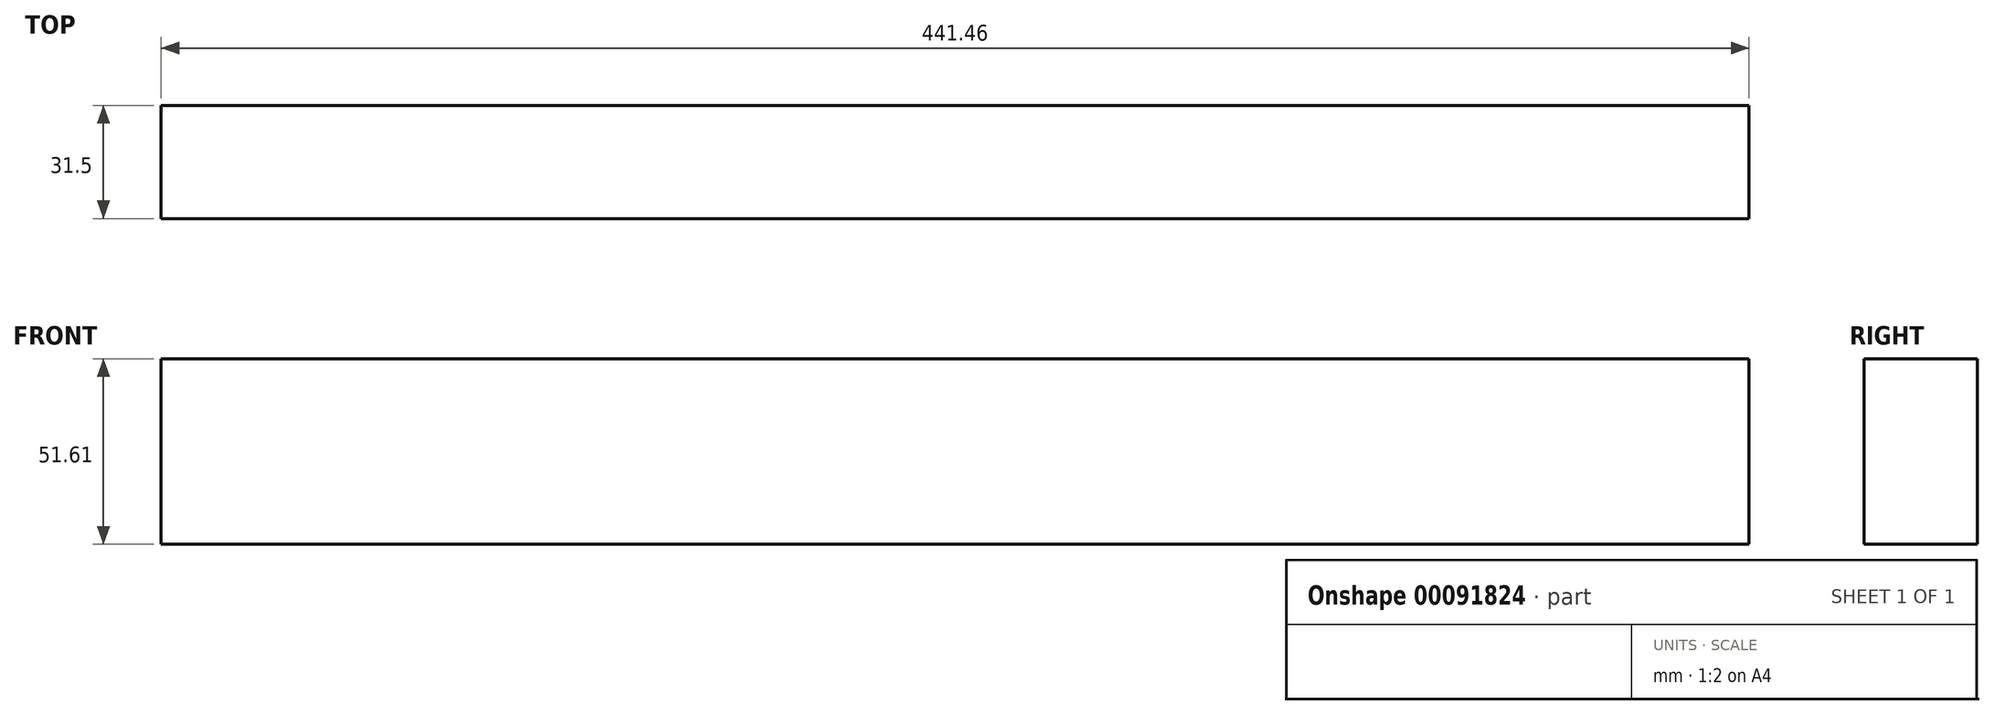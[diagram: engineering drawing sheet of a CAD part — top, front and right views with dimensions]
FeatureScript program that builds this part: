
annotation { "Feature Type Name" : "Feature", "Feature Type Description" : "" }
export const myFeature = defineFeature(function(context is Context, id is Id, definition is map)
    precondition{}
    {
        {
            var Q0;
            Q0=qCreatedBy(makeId("Top.planeOp"),FACE);
            var sketch = newSketch(context, id + "F0", { "sketchPlane" : qUnion([Q0])});
            skLineSegment(sketch, "E0.bottom", {"start": v(220.73, -15.75) * mm, "end": v(-220.73, -15.75) * mm});
            skLineSegment(sketch, "E0.top", {"start": v(220.73, 15.75) * mm, "end": v(-220.73, 15.75) * mm});
            skLineSegment(sketch, "E0.left", {"start": v(220.73, -15.75) * mm, "end": v(220.73, 15.75) * mm});
            skLineSegment(sketch, "E0.right", {"start": v(-220.73, -15.75) * mm, "end": v(-220.73, 15.75) * mm});
            skPoint(sketch, "E0.middle", {"position": v(0, 0) * mm});
            skSolve(sketch);
        }
        {
            var Q0;
            Q0 = qSketchRegion(id + "F0", true);
            extrude(context, id + "F1", {"entities" : qUnion([Q0]), "depth" : 51.6 * mm});
        }
    });
